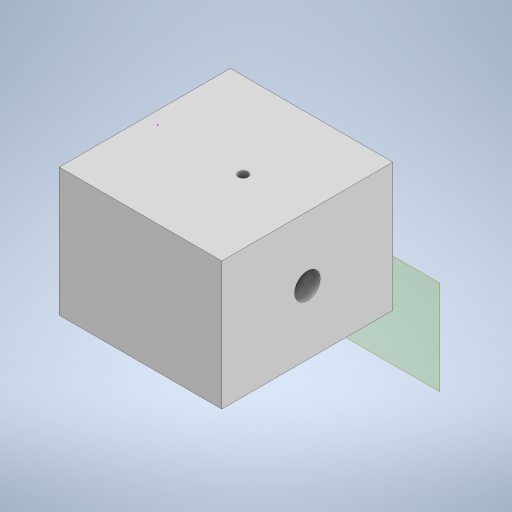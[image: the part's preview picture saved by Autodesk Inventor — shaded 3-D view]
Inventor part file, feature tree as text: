
AUTODESK INVENTOR PART (.ipt)
format: ipt  version: 2023 (Build 270158000, 158)  size: 288,768 bytes
history: native  units: mm
features: sketch x9, extrude x7, plane x6
ambient origin geometry x8: Origin, YZ Plane, XZ Plane, XY Plane, X Axis, Y Axis, Z Axis, Center Point
bodies: Body1 (feature_tree)
feature tree (22):
  plane  "Work Plane13"
  extrude  "Extrusion34"  Depth=40.0mm
  sketch  "Sketch46"  dims[d144=30.0mm d145=0.0mm d146=36.0mm]
  plane  "Work Plane11"
  extrude  "Extrusion35"  Depth=36.0mm
  sketch  "Sketch48"  dims[d150=0.0mm d151=0.0mm d156=20.0mm]
  extrude  "Extrusion36"  Depth=2.2mm
  plane  "Work Plane7"
  extrude  "Extrusion38"  Depth=20.0mm
  plane  "Work Plane4"
  extrude  "Extrusion39"  Depth=15.0mm TaperAngle=0.0deg
  plane  "Work Plane1"
  plane  "Work Plane6"
  extrude  "Extrusion42"  Depth=20.0mm
  extrude  "Extrusion44"  Depth=6.0mm
  sketch  "Sketch45"  dims[d142=38.0mm d143=40.0mm]
  sketch  "Sketch47"  dims[d147=30.0mm d148=-2.617994mm d149=2.2mm]
  sketch  "Sketch49"  dims[d157=15.0mm d158=15.0mm d159=0.0mm]
  sketch  "Sketch58"  dims[d160=4.0mm d161=20.0mm]
  sketch  "Sketch59"  dims[d162=35.0mm d163=0.0mm d172=6.0mm]
  sketch  "Sketch62"  dims[d173=0.0mm d174=0.0mm]
  sketch  "Sketch65"  dims[d177=5.0mm d178=0.0mm d49=0.5mm d50=0.872665mm d51=0.5mm d52=0.872665mm d130=0.5mm d131=0.872665mm d132=0.5mm d133=0.872665mm]
